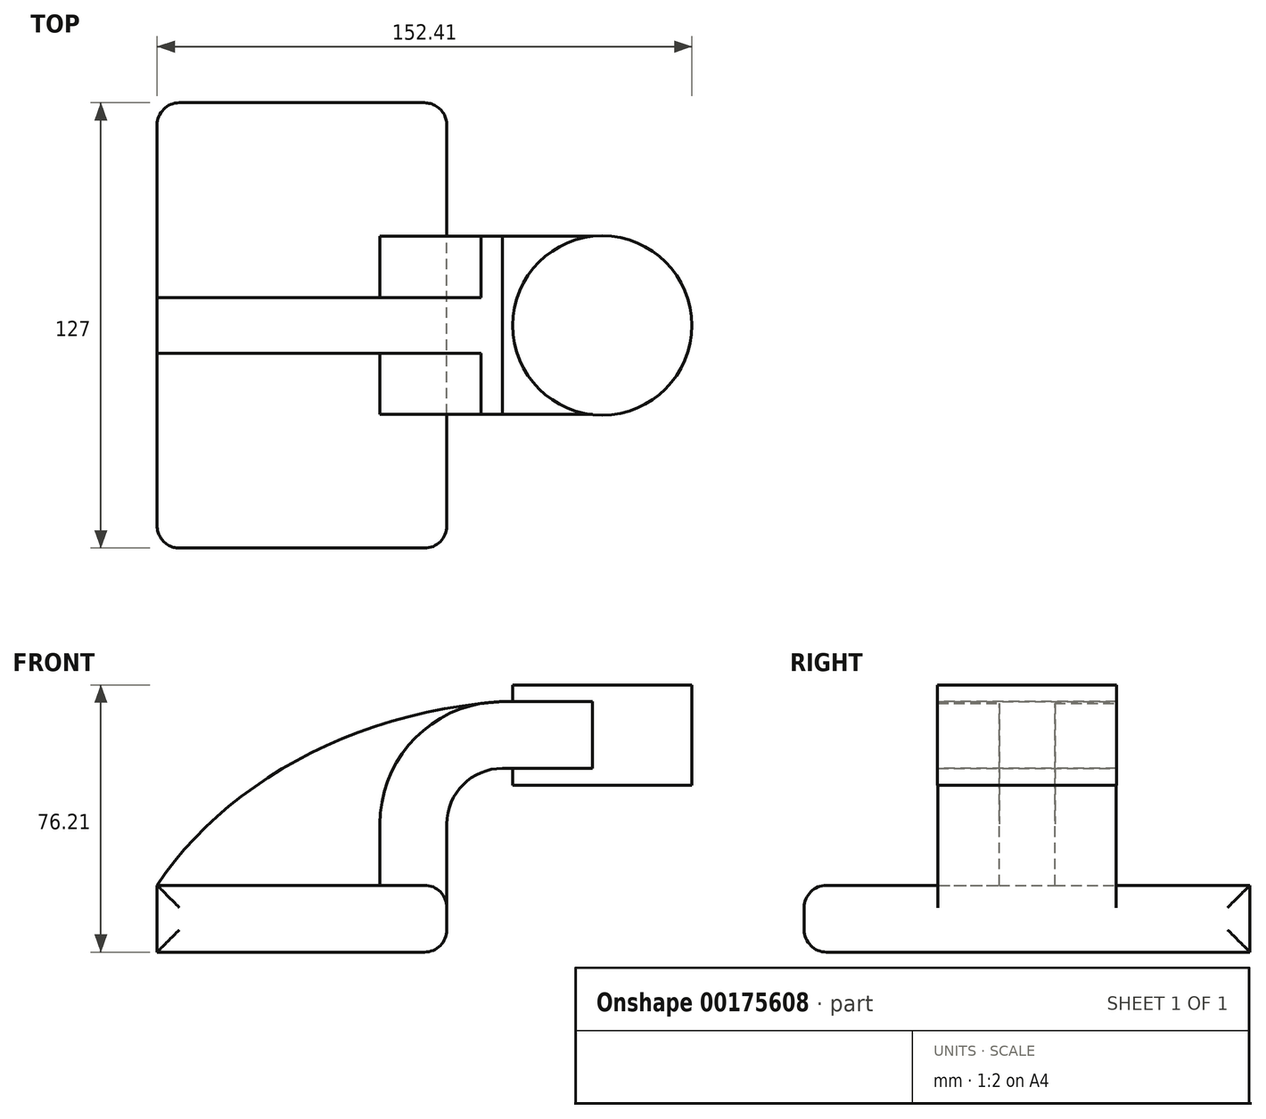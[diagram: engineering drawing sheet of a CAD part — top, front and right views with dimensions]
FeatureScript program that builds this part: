
annotation { "Feature Type Name" : "Feature", "Feature Type Description" : "" }
export const myFeature = defineFeature(function(context is Context, id is Id, definition is map)
    precondition{}
    {
        {
            var Q0;
            Q0=qCreatedBy(makeId("Front.planeOp"),FACE);
            var sketch = newSketch(context, id + "F0", { "sketchPlane" : qUnion([Q0])});
            skLineSegment(sketch, "E0.bottom", {"start": v(41.28, -9.52) * mm, "end": v(-41.28, -9.53) * mm});
            skLineSegment(sketch, "E0.top", {"start": v(41.28, 9.53) * mm, "end": v(-41.28, 9.53) * mm});
            skLineSegment(sketch, "E0.left", {"start": v(41.28, -9.52) * mm, "end": v(41.28, 9.53) * mm});
            skLineSegment(sketch, "E0.right", {"start": v(-41.28, -9.53) * mm, "end": v(-41.28, 9.53) * mm});
            skPoint(sketch, "E0.middle", {"position": v(0, 0) * mm});
            skLineSegment(sketch, "E1.bottom", {"start": v(111.12, 38.1) * mm, "end": v(60.33, 38.1) * mm});
            skLineSegment(sketch, "E1.top", {"start": v(111.12, 66.68) * mm, "end": v(60.33, 66.68) * mm});
            skLineSegment(sketch, "E1.left", {"start": v(111.12, 38.1) * mm, "end": v(111.12, 66.68) * mm});
            skLineSegment(sketch, "E1.right", {"start": v(60.33, 38.1) * mm, "end": v(60.33, 66.68) * mm});
            skPoint(sketch, "E1.middle", {"position": v(85.72, 52.39) * mm});
            skLineSegment(sketch, "E2", {"start": v(41.28, 9.53) * mm, "end": v(41.28, 27) * mm});
            skArc(sketch, "E3", {"start": v(41.27, 27) * mm, "mid": v(45.92, 38.23) * mm, "end": v(57.15, 42.88) * mm});
            skLineSegment(sketch, "E4", {"start": v(57.15, 42.88) * mm, "end": v(85.57, 42.88) * mm});
            skLineSegment(sketch, "E5.0", {"start": v(57.15, 61.93) * mm, "end": v(85.57, 61.93) * mm});
            skArc(sketch, "E5.1", {"start": v(22.23, 27) * mm, "mid": v(32.45, 51.7) * mm, "end": v(57.15, 61.93) * mm});
            skLineSegment(sketch, "E5.2", {"start": v(22.22, 9.53) * mm, "end": v(22.22, 27) * mm});
            skPoint(sketch, "E6.endSnap0", {"position": v(85.72, 66.68) * mm});
            skFitSpline(sketch, "E7", {"points": [v(-41.28, 9.53) * mm, v(57.15, 61.93) * mm], "startDerivative": vector(56.1, 84.77) * mm, "endDerivative": vector(129.98, 8.85) * mm});
            skLineSegment(sketch, "E8", {"start": v(85.57, 66.68) * mm, "end": v(85.57, 38.1) * mm});
            skSolve(sketch);
        }
        {
            var Q0;
            Q0=makeQuery(id+"F0.imprint","IMPRINT",FACE,{"disambiguationData":[TD([[makeQuery(id+"F0.imprint","IMPRINT",EDGE,{"derivedFrom":sQuery(id+"F0.wireOp",EDGE,"E0.bottom")}),-1.0]])]});
            extrude(context, id + "F1", {"entities" : qUnion([Q0]), "endBound" : BoundingType.SYMMETRIC, "depth" : 127 * mm});
        }
        {
            var Q0;
            {var subQ3=sQuery(id+"F0.wireOp",EDGE,"E5.2");Q0=makeQuery(id+"F0.imprint","IMPRINT",FACE,{"disambiguationData":[TD([[makeQuery(id+"F0.imprint","IMPRINT",EDGE,{"derivedFrom":subQ3}),1.0]])]});}
            extrude(context, id + "F2", {"entities" : qUnion([Q0]), "operationType" : NewBodyOperationType.ADD, "endBound" : BoundingType.SYMMETRIC, "depth" : 15.88 * mm});
        }
        {
            var Q0;
            {var subQ1=sQuery(id+"F0.wireOp",EDGE,"E2");Q0=makeQuery(id+"F0.imprint","IMPRINT",FACE,{"disambiguationData":[TD([[makeQuery(id+"F0.imprint","IMPRINT",EDGE,{"derivedFrom":subQ1}),1.0]])]});}
            var Q1;
            {var subQ5=sQuery(id+"F0.wireOp",EDGE,"aUzpnZX3-ESaH-eppK-CBqX-7Jh1ZbWJmEzc");Q1=makeQuery(id+"F0.imprint","IMPRINT",FACE,{"disambiguationData":[TD([[makeQuery(id+"F0.imprint","IMPRINT",EDGE,{"derivedFrom":subQ5}),-1.0]])]});}
            var Q2;
            {var subQ0=sQuery(id+"F0.wireOp",EDGE,"E4");var subQ1=sQuery(id+"F0.wireOp",EDGE,"E1.right");var subQ2=makeQuery(id+"F0.imprint","INTERSECT",VERTEX,{"derivedFrom":[subQ1,subQ0]});Q2=makeQuery(id+"F0.imprint","IMPRINT",FACE,{"disambiguationData":[TD([[makeQuery(id+"F0.imprint","IMPRINT",EDGE,{"disambiguationData":[TD([[subQ2,-1.0]])],"derivedFrom":subQ1}),-1.0]])]});}
            extrude(context, id + "F3", {"entities" : qUnion([Q0, Q1, Q2]), "operationType" : NewBodyOperationType.ADD, "endBound" : BoundingType.SYMMETRIC, "depth" : 50.8 * mm});
        }
        {
            var Q0;
            {var subQ4=sQuery(id+"F0.wireOp",EDGE,"E1.left");Q0=makeQuery(id+"F0.imprint","IMPRINT",FACE,{"disambiguationData":[TD([[makeQuery(id+"F0.imprint","IMPRINT",EDGE,{"derivedFrom":subQ4}),1.0]])]});}
            var Q1;
            Q1=sQuery(id+"F0.wireOp",EDGE,"E8");
            revolve(context, id + "F4", {"operationType" : NewBodyOperationType.ADD, "entities" : qUnion([Q0]), "axis" : qUnion([Q1]), "revolveType" : RevolveType.FULL});
        }
        {
            var Q0;
            Q0=makeQuery(id+"F1.opExtrude","CAP_EDGE",EDGE,{"disambiguationData":[OSD([sQuery(id+"F0.wireOp",EDGE,"E0.left")])],"isStart":false});
            var Q1;
            Q1=makeQuery(id+"F1.opExtrude","CAP_EDGE",EDGE,{"disambiguationData":[OSD([sQuery(id+"F0.wireOp",EDGE,"E0.right")])],"isStart":false});
            var Q2;
            Q2=makeQuery(id+"F1.opExtrude","CAP_EDGE",EDGE,{"disambiguationData":[OSD([sQuery(id+"F0.wireOp",EDGE,"E0.top")])],"isStart":false});
            var Q3;
            Q3=makeQuery(id+"F1.opExtrude","SWEPT_EDGE",EDGE,{"disambiguationData":[OSD([sQuery(id+"F0.wireOp",EDGE,"E0.bottom"),sQuery(id+"F0.wireOp",EDGE,"E0.left")])]});
            var Q4;
            Q4=makeQuery(id+"F1.opExtrude","CAP_EDGE",EDGE,{"disambiguationData":[OSD([sQuery(id+"F0.wireOp",EDGE,"E0.bottom")])],"isStart":false});
            var Q5;
            {var subQ0=sQuery(id+"F0.wireOp",EDGE,"E2");var subQ1=sQuery(id+"F0.wireOp",EDGE,"E0.top");var subQ2=sQuery(id+"F0.wireOp",EDGE,"E0.left");Q5=makeQuery(id+"F3.boolean.opBoolean","SPLIT",EDGE,{"disambiguationData":[TD([makeQuery(id+"F1.opExtrude","CAP_FACE",FACE,{"disambiguationData":[OSD([sQuery(id+"F0.wireOp",EDGE,"E0.bottom"),subQ1,subQ2,sQuery(id+"F0.wireOp",EDGE,"E0.right")])],"isStart":false})])],"derivedFrom":makeQuery(id+"F1.opExtrude","SWEPT_EDGE",EDGE,{"disambiguationData":[OSD([subQ1,subQ2,subQ0])]})});}
            var Q6;
            Q6=makeQuery(id+"F1.opExtrude","CAP_EDGE",EDGE,{"disambiguationData":[OSD([sQuery(id+"F0.wireOp",EDGE,"E0.right")])],"isStart":true});
            var Q7;
            Q7=makeQuery(id+"F1.opExtrude","CAP_EDGE",EDGE,{"disambiguationData":[OSD([sQuery(id+"F0.wireOp",EDGE,"E0.left")])],"isStart":true});
            fillet(context, id + "F5", {"entities" : qUnion([Q0, Q1, Q2, Q3, Q4, Q5, Q6, Q7]), "radius" : 6.35 * mm, "tangentPropagation" : true, "allowEdgeOverflow" : false});
        }
    });
